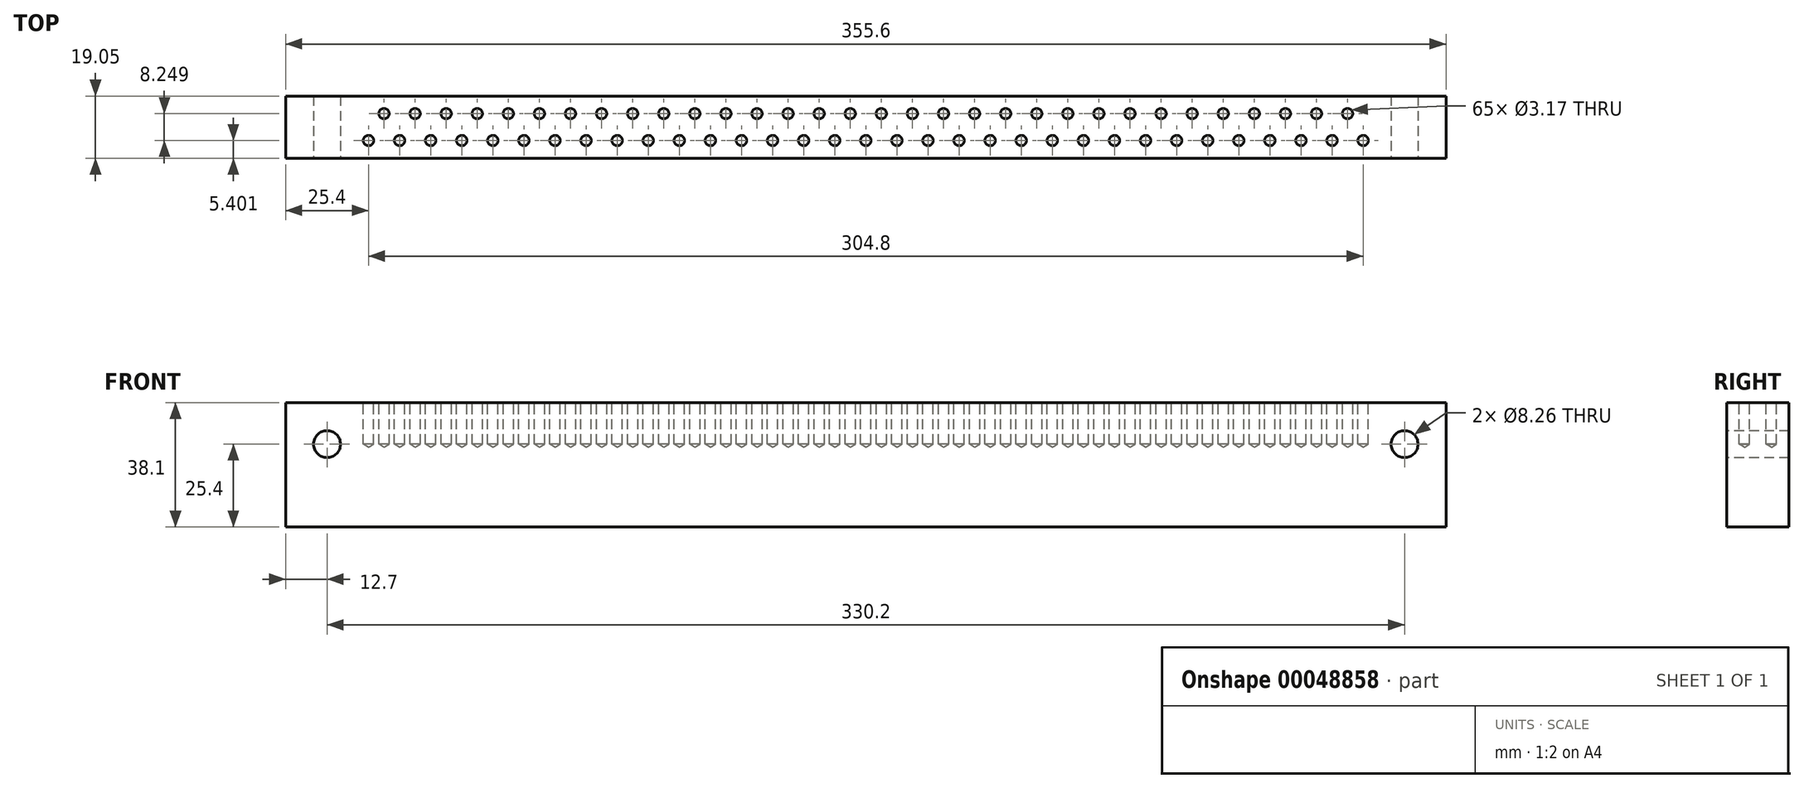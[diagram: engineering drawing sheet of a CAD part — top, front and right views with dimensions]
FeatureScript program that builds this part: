
annotation { "Feature Type Name" : "Feature", "Feature Type Description" : "" }
export const myFeature = defineFeature(function(context is Context, id is Id, definition is map)
    precondition{}
    {
        {
            var Q0;
            Q0=qCreatedBy(makeId("Top.planeOp"),FACE);
            var sketch = newSketch(context, id + "F0", { "sketchPlane" : qUnion([Q0])});
            skLineSegment(sketch, "E0", {"start": v(0, 0) * mm, "end": v(177.8, 0) * mm});
            skLineSegment(sketch, "E1", {"start": v(177.8, 0) * mm, "end": v(177.8, 19.05) * mm});
            skLineSegment(sketch, "E2", {"start": v(177.8, 19.05) * mm, "end": v(-177.8, 19.05) * mm});
            skLineSegment(sketch, "E3", {"start": v(-177.8, 19.05) * mm, "end": v(-177.8, 0) * mm});
            skLineSegment(sketch, "E4", {"start": v(-177.8, 0) * mm, "end": v(0, 0) * mm});
            skSolve(sketch);
        }
        {
            var Q0;
            Q0=makeQuery(id+"F0.imprint","IMPRINT",FACE,{"disambiguationData":[TD([[makeQuery(id+"F0.imprint","IMPRINT",EDGE,{"derivedFrom":sQuery(id+"F0.wireOp",EDGE,"E0")}),1.0]])]});
            extrude(context, id + "F1", {"entities" : qUnion([Q0]), "depth" : 38.1 * mm});
        }
        {
            var Q0;
            Q0=makeQuery(id+"F1.opExtrude","CAP_FACE",FACE,{"disambiguationData":[OSD([sQuery(id+"F0.wireOp",EDGE,"E0"),sQuery(id+"F0.wireOp",EDGE,"E1"),sQuery(id+"F0.wireOp",EDGE,"E2"),sQuery(id+"F0.wireOp",EDGE,"E3"),sQuery(id+"F0.wireOp",EDGE,"E4")])],"isStart":false});
            var sketch = newSketch(context, id + "F2", { "sketchPlane" : qUnion([Q0])});
            skPoint(sketch, "E5", {"position": v(0, 5.4) * mm});
            skPoint(sketch, "E6.1.0.0", {"position": v(9.53, 5.4) * mm});
            skPoint(sketch, "E6.2.0.0", {"position": v(19.05, 5.4) * mm});
            skPoint(sketch, "E6.3.0.0", {"position": v(28.58, 5.4) * mm});
            skPoint(sketch, "E6.4.0.0", {"position": v(38.1, 5.4) * mm});
            skPoint(sketch, "E6.5.0.0", {"position": v(47.62, 5.4) * mm});
            skPoint(sketch, "E6.6.0.0", {"position": v(57.15, 5.4) * mm});
            skPoint(sketch, "E6.7.0.0", {"position": v(66.67, 5.4) * mm});
            skPoint(sketch, "E6.8.0.0", {"position": v(76.2, 5.4) * mm});
            skPoint(sketch, "E6.9.0.0", {"position": v(85.73, 5.4) * mm});
            skPoint(sketch, "E6.10.0.0", {"position": v(95.25, 5.4) * mm});
            skPoint(sketch, "E6.11.0.0", {"position": v(104.78, 5.4) * mm});
            skPoint(sketch, "E6.12.0.0", {"position": v(114.3, 5.4) * mm});
            skPoint(sketch, "E6.13.0.0", {"position": v(123.83, 5.4) * mm});
            skPoint(sketch, "E6.14.0.0", {"position": v(133.35, 5.4) * mm});
            skPoint(sketch, "E6.15.0.0", {"position": v(142.88, 5.4) * mm});
            skPoint(sketch, "E6.16.0.0", {"position": v(152.4, 5.4) * mm});
            skLineSegment(sketch, "E6.direction1", {"start": v(0, 5.4) * mm, "end": v(9.53, 5.4) * mm, "construction": true});
            skPoint(sketch, "E7.1.0.0", {"position": v(-9.53, 5.4) * mm});
            skPoint(sketch, "E7.2.0.0", {"position": v(-19.05, 5.4) * mm});
            skPoint(sketch, "E7.3.0.0", {"position": v(-28.58, 5.4) * mm});
            skPoint(sketch, "E7.4.0.0", {"position": v(-38.1, 5.4) * mm});
            skPoint(sketch, "E7.5.0.0", {"position": v(-47.62, 5.4) * mm});
            skPoint(sketch, "E7.6.0.0", {"position": v(-57.15, 5.4) * mm});
            skPoint(sketch, "E7.7.0.0", {"position": v(-66.67, 5.4) * mm});
            skPoint(sketch, "E7.8.0.0", {"position": v(-76.2, 5.4) * mm});
            skPoint(sketch, "E7.9.0.0", {"position": v(-85.73, 5.4) * mm});
            skPoint(sketch, "E7.10.0.0", {"position": v(-95.25, 5.4) * mm});
            skPoint(sketch, "E7.11.0.0", {"position": v(-104.78, 5.4) * mm});
            skPoint(sketch, "E7.12.0.0", {"position": v(-114.3, 5.4) * mm});
            skPoint(sketch, "E7.13.0.0", {"position": v(-123.83, 5.4) * mm});
            skPoint(sketch, "E7.14.0.0", {"position": v(-133.35, 5.4) * mm});
            skPoint(sketch, "E7.15.0.0", {"position": v(-142.88, 5.4) * mm});
            skPoint(sketch, "E7.16.0.0", {"position": v(-152.4, 5.4) * mm});
            skLineSegment(sketch, "E7.direction1", {"start": v(0, 5.4) * mm, "end": v(-9.53, 5.4) * mm, "construction": true});
            skPoint(sketch, "E8", {"position": v(-147.64, 13.65) * mm});
            skPoint(sketch, "E9.1.0.0", {"position": v(-138.11, 13.65) * mm});
            skPoint(sketch, "E9.2.0.0", {"position": v(-128.59, 13.65) * mm});
            skPoint(sketch, "E9.3.0.0", {"position": v(-119.06, 13.65) * mm});
            skPoint(sketch, "E9.4.0.0", {"position": v(-109.54, 13.65) * mm});
            skPoint(sketch, "E9.5.0.0", {"position": v(-100.01, 13.65) * mm});
            skPoint(sketch, "E9.6.0.0", {"position": v(-90.49, 13.65) * mm});
            skPoint(sketch, "E9.7.0.0", {"position": v(-80.96, 13.65) * mm});
            skPoint(sketch, "E9.8.0.0", {"position": v(-71.44, 13.65) * mm});
            skPoint(sketch, "E9.9.0.0", {"position": v(-61.91, 13.65) * mm});
            skPoint(sketch, "E9.10.0.0", {"position": v(-52.39, 13.65) * mm});
            skPoint(sketch, "E9.11.0.0", {"position": v(-42.86, 13.65) * mm});
            skPoint(sketch, "E9.12.0.0", {"position": v(-33.34, 13.65) * mm});
            skPoint(sketch, "E9.13.0.0", {"position": v(-23.81, 13.65) * mm});
            skPoint(sketch, "E9.14.0.0", {"position": v(-14.29, 13.65) * mm});
            skPoint(sketch, "E9.15.0.0", {"position": v(-4.76, 13.65) * mm});
            skPoint(sketch, "E9.16.0.0", {"position": v(4.76, 13.65) * mm});
            skPoint(sketch, "E9.17.0.0", {"position": v(14.29, 13.65) * mm});
            skPoint(sketch, "E9.18.0.0", {"position": v(23.81, 13.65) * mm});
            skPoint(sketch, "E9.19.0.0", {"position": v(33.34, 13.65) * mm});
            skPoint(sketch, "E9.20.0.0", {"position": v(42.86, 13.65) * mm});
            skPoint(sketch, "E9.21.0.0", {"position": v(52.39, 13.65) * mm});
            skPoint(sketch, "E9.22.0.0", {"position": v(61.91, 13.65) * mm});
            skPoint(sketch, "E9.23.0.0", {"position": v(71.44, 13.65) * mm});
            skPoint(sketch, "E9.24.0.0", {"position": v(80.96, 13.65) * mm});
            skPoint(sketch, "E9.25.0.0", {"position": v(90.49, 13.65) * mm});
            skPoint(sketch, "E9.26.0.0", {"position": v(100.01, 13.65) * mm});
            skPoint(sketch, "E9.27.0.0", {"position": v(109.54, 13.65) * mm});
            skPoint(sketch, "E9.28.0.0", {"position": v(119.06, 13.65) * mm});
            skPoint(sketch, "E9.29.0.0", {"position": v(128.59, 13.65) * mm});
            skPoint(sketch, "E9.30.0.0", {"position": v(138.11, 13.65) * mm});
            skPoint(sketch, "E9.31.0.0", {"position": v(147.64, 13.65) * mm});
            skLineSegment(sketch, "E9.direction1", {"start": v(-147.64, 13.65) * mm, "end": v(-138.11, 13.65) * mm, "construction": true});
            skSolve(sketch);
        }
        {
            var Q0;
            Q0=sQuery(id+"F2.wireOp",VERTEX,"E7.10.0.0");
            var Q1;
            Q1=sQuery(id+"F2.wireOp",VERTEX,"E9.18.0.0");
            var Q2;
            Q2=sQuery(id+"F2.wireOp",VERTEX,"E7.8.0.0");
            var Q3;
            Q3=sQuery(id+"F2.wireOp",VERTEX,"E9.9.0.0");
            var Q4;
            Q4=sQuery(id+"F2.wireOp",VERTEX,"E7.5.0.0");
            var Q5;
            Q5=sQuery(id+"F2.wireOp",VERTEX,"E9.2.0.0");
            var Q6;
            Q6=sQuery(id+"F2.wireOp",VERTEX,"E9.30.0.0");
            var Q7;
            Q7=sQuery(id+"F2.wireOp",VERTEX,"E9.23.0.0");
            var Q8;
            Q8=sQuery(id+"F2.wireOp",VERTEX,"E9.25.0.0");
            var Q9;
            Q9=sQuery(id+"F2.wireOp",VERTEX,"E9.4.0.0");
            var Q10;
            Q10=sQuery(id+"F2.wireOp",VERTEX,"E7.13.0.0");
            var Q11;
            Q11=sQuery(id+"F2.wireOp",VERTEX,"E9.26.0.0");
            var Q12;
            Q12=sQuery(id+"F2.wireOp",VERTEX,"E9.20.0.0");
            var Q13;
            Q13=sQuery(id+"F2.wireOp",VERTEX,"E7.3.0.0");
            var Q14;
            Q14=sQuery(id+"F2.wireOp",VERTEX,"E9.12.0.0");
            var Q15;
            Q15=sQuery(id+"F2.wireOp",VERTEX,"E8");
            var Q16;
            Q16=sQuery(id+"F2.wireOp",VERTEX,"E6.15.0.0");
            var Q17;
            Q17=sQuery(id+"F2.wireOp",VERTEX,"E6.11.0.0");
            var Q18;
            Q18=sQuery(id+"F2.wireOp",VERTEX,"E9.10.0.0");
            var Q19;
            Q19=sQuery(id+"F2.wireOp",VERTEX,"E7.11.0.0");
            var Q20;
            Q20=sQuery(id+"F2.wireOp",VERTEX,"E9.21.0.0");
            var Q21;
            Q21=sQuery(id+"F2.wireOp",VERTEX,"E9.5.0.0");
            var Q22;
            Q22=sQuery(id+"F2.wireOp",VERTEX,"E7.6.0.0");
            var Q23;
            Q23=sQuery(id+"F2.wireOp",VERTEX,"E9.19.0.0");
            var Q24;
            Q24=sQuery(id+"F2.wireOp",VERTEX,"E9.3.0.0");
            var Q25;
            Q25=sQuery(id+"F2.wireOp",VERTEX,"E7.4.0.0");
            var Q26;
            Q26=sQuery(id+"F2.wireOp",VERTEX,"E6.1.0.0");
            var Q27;
            Q27=sQuery(id+"F2.wireOp",VERTEX,"E6.2.0.0");
            var Q28;
            Q28=sQuery(id+"F2.wireOp",VERTEX,"E6.3.0.0");
            var Q29;
            Q29=sQuery(id+"F2.wireOp",VERTEX,"E6.4.0.0");
            var Q30;
            Q30=sQuery(id+"F2.wireOp",VERTEX,"E6.5.0.0");
            var Q31;
            Q31=sQuery(id+"F2.wireOp",VERTEX,"E6.6.0.0");
            var Q32;
            Q32=sQuery(id+"F2.wireOp",VERTEX,"E9.7.0.0");
            var Q33;
            Q33=sQuery(id+"F2.wireOp",VERTEX,"E6.13.0.0");
            var Q34;
            Q34=sQuery(id+"F2.wireOp",VERTEX,"E7.1.0.0");
            var Q35;
            Q35=sQuery(id+"F2.wireOp",VERTEX,"E9.14.0.0");
            var Q36;
            Q36=sQuery(id+"F2.wireOp",VERTEX,"E7.15.0.0");
            var Q37;
            Q37=sQuery(id+"F2.wireOp",VERTEX,"E9.28.0.0");
            var Q38;
            Q38=sQuery(id+"F2.wireOp",VERTEX,"E9.16.0.0");
            var Q39;
            Q39=sQuery(id+"F2.wireOp",VERTEX,"E9.17.0.0");
            var Q40;
            Q40=sQuery(id+"F2.wireOp",VERTEX,"E9.1.0.0");
            var Q41;
            Q41=sQuery(id+"F2.wireOp",VERTEX,"E7.2.0.0");
            var Q42;
            Q42=sQuery(id+"F2.wireOp",VERTEX,"E6.16.0.0");
            var Q43;
            Q43=sQuery(id+"F2.wireOp",VERTEX,"E9.24.0.0");
            var Q44;
            Q44=sQuery(id+"F2.wireOp",VERTEX,"E9.31.0.0");
            var Q45;
            Q45=sQuery(id+"F2.wireOp",VERTEX,"E9.8.0.0");
            var Q46;
            Q46=sQuery(id+"F2.wireOp",VERTEX,"E9.15.0.0");
            var Q47;
            Q47=sQuery(id+"F2.wireOp",VERTEX,"E7.16.0.0");
            var Q48;
            Q48=sQuery(id+"F2.wireOp",VERTEX,"E7.9.0.0");
            var Q49;
            Q49=sQuery(id+"F2.wireOp",VERTEX,"E6.14.0.0");
            var Q50;
            Q50=sQuery(id+"F2.wireOp",VERTEX,"E6.7.0.0");
            var Q51;
            Q51=sQuery(id+"F2.wireOp",VERTEX,"E9.22.0.0");
            var Q52;
            Q52=sQuery(id+"F2.wireOp",VERTEX,"E9.29.0.0");
            var Q53;
            Q53=sQuery(id+"F2.wireOp",VERTEX,"E9.6.0.0");
            var Q54;
            Q54=sQuery(id+"F2.wireOp",VERTEX,"E9.13.0.0");
            var Q55;
            Q55=sQuery(id+"F2.wireOp",VERTEX,"E7.14.0.0");
            var Q56;
            Q56=sQuery(id+"F2.wireOp",VERTEX,"E7.7.0.0");
            var Q57;
            Q57=sQuery(id+"F2.wireOp",VERTEX,"E6.12.0.0");
            var Q58;
            Q58=sQuery(id+"F2.wireOp",VERTEX,"E6.8.0.0");
            var Q59;
            Q59=sQuery(id+"F2.wireOp",VERTEX,"E6.9.0.0");
            var Q60;
            Q60=sQuery(id+"F2.wireOp",VERTEX,"E9.27.0.0");
            var Q61;
            Q61=sQuery(id+"F2.wireOp",VERTEX,"E9.11.0.0");
            var Q62;
            Q62=sQuery(id+"F2.wireOp",VERTEX,"E7.12.0.0");
            var Q63;
            Q63=sQuery(id+"F2.wireOp",VERTEX,"E6.10.0.0");
            var Q64;
            Q64=sQuery(id+"F2.wireOp",VERTEX,"E7.direction1.start");
            var Q65;
            Q65=makeQuery(id+"F1.opExtrude","SWEPT_BODY",BODY,{"disambiguationData":[OSD([sQuery(id+"F0.wireOp",EDGE,"E0"),sQuery(id+"F0.wireOp",EDGE,"E1"),sQuery(id+"F0.wireOp",EDGE,"E2"),sQuery(id+"F0.wireOp",EDGE,"E3"),sQuery(id+"F0.wireOp",EDGE,"E4")])]});
            hole(context, id + "F3", {"style" : HoleStyle.SIMPLE, "holeDiameter" : 3.17 * mm, "endStyle" : HoleEndStyle.BLIND, "holeDepth" : 12.7 * mm, "locations" : qUnion([Q0, Q1, Q2, Q3, Q4, Q5, Q6, Q7, Q8, Q9, Q10, Q11, Q12, Q13, Q14, Q15, Q16, Q17, Q18, Q19, Q20, Q21, Q22, Q23, Q24, Q25, Q26, Q27, Q28, Q29, Q30, Q31, Q32, Q33, Q34, Q35, Q36, Q37, Q38, Q39, Q40, Q41, Q42, Q43, Q44, Q45, Q46, Q47, Q48, Q49, Q50, Q51, Q52, Q53, Q54, Q55, Q56, Q57, Q58, Q59, Q60, Q61, Q62, Q63, Q64]), "scope" : qUnion([Q65])});
        }
        {
            var Q0;
            Q0=makeQuery(id+"F1.opExtrude","SWEPT_FACE",FACE,{"disambiguationData":[OSD([sQuery(id+"F0.wireOp",EDGE,"E0"),sQuery(id+"F0.wireOp",EDGE,"E4")])]});
            var sketch = newSketch(context, id + "F4", { "sketchPlane" : qUnion([Q0])});
            skPoint(sketch, "E10", {"position": v(165.1, 25.4) * mm});
            skPoint(sketch, "E11", {"position": v(0, 0) * mm});
            skLineSegment(sketch, "E12", {"start": v(0, 0) * mm, "end": v(0, 48.9) * mm, "construction": true});
            skPoint(sketch, "E12.endSnap0", {"position": v(0, 38.1) * mm});
            skPoint(sketch, "E13.MirrorP", {"position": v(-165.1, 25.4) * mm});
            skSolve(sketch);
        }
        {
            var Q0;
            Q0=sQuery(id+"F4.wireOp",VERTEX,"E13.MirrorP");
            var Q1;
            Q1=sQuery(id+"F4.wireOp",VERTEX,"E10");
            var Q2;
            Q2=makeQuery(id+"F1.opExtrude","SWEPT_BODY",BODY,{"disambiguationData":[OSD([sQuery(id+"F0.wireOp",EDGE,"E0"),sQuery(id+"F0.wireOp",EDGE,"E1"),sQuery(id+"F0.wireOp",EDGE,"E2"),sQuery(id+"F0.wireOp",EDGE,"E3"),sQuery(id+"F0.wireOp",EDGE,"E4")])]});
            hole(context, id + "F5", {"style" : HoleStyle.SIMPLE, "holeDiameter" : 8.25 * mm, "endStyle" : HoleEndStyle.THROUGH, "locations" : qUnion([Q0, Q1]), "scope" : qUnion([Q2])});
        }
    });
